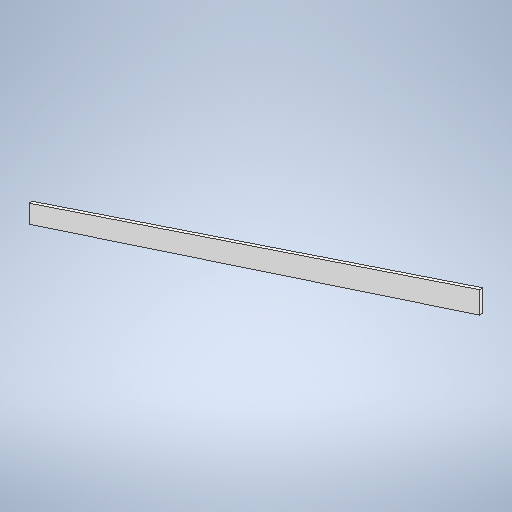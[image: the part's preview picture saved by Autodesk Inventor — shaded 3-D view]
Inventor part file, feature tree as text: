
AUTODESK INVENTOR PART (.ipt)
format: ipt  version: 2025.1 (Build 291241020, 241B)  size: 263,680 bytes
history: native  units: in
note: dims shown in document units (in); Inventor stores cm internally (conversion verified against a paired STEP export)
features: extrude x1, plane x1, sketch x1
ambient origin geometry x8: Origin, YZ Plane, XZ Plane, XY Plane, X Axis, Y Axis, Z Axis, Center Point
bodies: Body1 (feature_tree)
feature tree (3):
  extrude  "Extrusion2"  Depth=1.0in
  plane  "Work Plane2"
  sketch  "Sketch1"  dims[d5=5.5in d17=3.5in d19=132.0in d23=2.2565in d28=1.8813in d33=42.875in d36=5.5in d37=6.653in d38=1.0in d39=0.0in d40=90.0deg]
